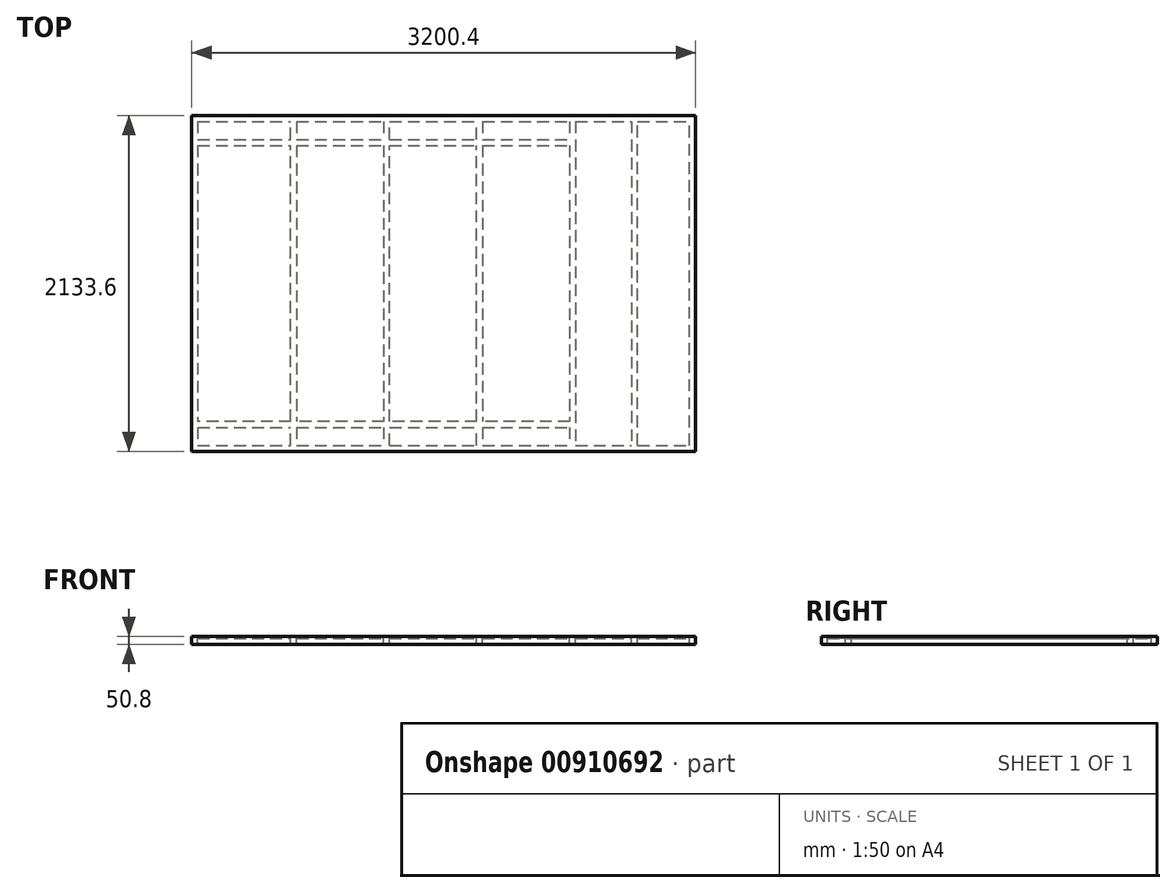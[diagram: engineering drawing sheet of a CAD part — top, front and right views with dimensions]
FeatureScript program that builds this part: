
annotation { "Feature Type Name" : "Feature", "Feature Type Description" : "" }
export const myFeature = defineFeature(function(context is Context, id is Id, definition is map)
    precondition{}
    {
        {
            var Q0;
            Q0=qCreatedBy(makeId("Top.planeOp"),FACE);
            var sketch = newSketch(context, id + "F0", { "sketchPlane" : qUnion([Q0])});
            skLineSegment(sketch, "E0.bottom", {"start": v(1600.2, 1066.8) * mm, "end": v(-1600.2, 1066.8) * mm});
            skLineSegment(sketch, "E0.top", {"start": v(1600.2, -1066.8) * mm, "end": v(-1600.2, -1066.8) * mm});
            skLineSegment(sketch, "E0.left", {"start": v(1600.2, 1066.8) * mm, "end": v(1600.2, -1066.8) * mm});
            skLineSegment(sketch, "E0.right", {"start": v(-1600.2, 1066.8) * mm, "end": v(-1600.2, -1066.8) * mm});
            skPoint(sketch, "E0.middle", {"position": v(0, 0) * mm});
            skLineSegment(sketch, "E1", {"start": v(-1600.2, -1066.8) * mm, "end": v(-381, -1066.8) * mm});
            skLineSegment(sketch, "E2", {"start": v(-381, -1066.8) * mm, "end": v(-381, -1028.7) * mm});
            skLineSegment(sketch, "E3", {"start": v(-381, 1066.8) * mm, "end": v(838.2, 1066.8) * mm});
            skLineSegment(sketch, "E4", {"start": v(838.2, 1066.8) * mm, "end": v(838.2, -1028.7) * mm});
            skLineSegment(sketch, "E5", {"start": v(-1600.2, -1028.7) * mm, "end": v(1600.2, -1028.7) * mm});
            skLineSegment(sketch, "E6", {"start": v(-1600.2, 1028.7) * mm, "end": v(1600.2, 1028.7) * mm});
            skLineSegment(sketch, "E7", {"start": v(-1562.1, 1028.7) * mm, "end": v(-1562.1, 914.4) * mm});
            skLineSegment(sketch, "E8", {"start": v(1562.1, -1028.7) * mm, "end": v(1562.1, 1028.7) * mm});
            skLineSegment(sketch, "E9", {"start": v(-1600.2, -1028.7) * mm, "end": v(-971.55, -1028.7) * mm});
            skLineSegment(sketch, "E10", {"start": v(-971.55, -1028.7) * mm, "end": v(-971.55, -914.4) * mm});
            skLineSegment(sketch, "E11", {"start": v(-933.45, 1028.7) * mm, "end": v(-933.45, 914.4) * mm});
            skLineSegment(sketch, "E12", {"start": v(-1600.2, 914.4) * mm, "end": v(838.2, 914.4) * mm});
            skLineSegment(sketch, "E13", {"start": v(-1600.2, 876.3) * mm, "end": v(838.2, 876.3) * mm});
            skLineSegment(sketch, "E14.trimOffspring", {"start": v(-971.55, 914.4) * mm, "end": v(-971.55, 1028.7) * mm});
            skLineSegment(sketch, "E15.trimOffspring", {"start": v(-933.45, 876.3) * mm, "end": v(-933.45, -876.3) * mm});
            skLineSegment(sketch, "E16.trimOffspring", {"start": v(-1562.1, 876.3) * mm, "end": v(-1562.1, -876.3) * mm});
            skLineSegment(sketch, "E17", {"start": v(-1600.2, -914.4) * mm, "end": v(838.2, -914.4) * mm});
            skLineSegment(sketch, "E18", {"start": v(838.2, -876.3) * mm, "end": v(-1600.2, -876.3) * mm});
            skLineSegment(sketch, "E19.trimOffspring", {"start": v(-933.45, -914.4) * mm, "end": v(-933.45, -1028.7) * mm});
            skLineSegment(sketch, "E20.trimOffspring", {"start": v(-971.55, -876.3) * mm, "end": v(-971.55, 876.3) * mm});
            skLineSegment(sketch, "E21.trimOffspring", {"start": v(-1562.1, -914.4) * mm, "end": v(-1562.1, -1028.7) * mm});
            skLineSegment(sketch, "E22", {"start": v(800.1, 1028.7) * mm, "end": v(800.1, 914.4) * mm});
            skLineSegment(sketch, "E23", {"start": v(247.65, 1028.7) * mm, "end": v(247.65, 914.4) * mm});
            skLineSegment(sketch, "E24", {"start": v(209.55, -1028.7) * mm, "end": v(209.55, -914.4) * mm});
            skLineSegment(sketch, "E25", {"start": v(-381, 1028.7) * mm, "end": v(-381, 914.4) * mm});
            skLineSegment(sketch, "E26", {"start": v(-342.9, -1028.7) * mm, "end": v(-342.9, -914.4) * mm});
            skLineSegment(sketch, "E27.trimOffspring", {"start": v(-381, 876.3) * mm, "end": v(-381, -876.3) * mm});
            skLineSegment(sketch, "E28.trimOffspring", {"start": v(-342.9, 914.4) * mm, "end": v(-342.9, 1028.7) * mm});
            skLineSegment(sketch, "E29.trimOffspring", {"start": v(-381, -914.4) * mm, "end": v(-381, -1028.7) * mm});
            skLineSegment(sketch, "E30.trimOffspring", {"start": v(-342.9, -876.3) * mm, "end": v(-342.9, 876.3) * mm});
            skLineSegment(sketch, "E31.trimOffspring", {"start": v(247.65, -914.4) * mm, "end": v(247.65, -1028.7) * mm});
            skLineSegment(sketch, "E32.trimOffspring", {"start": v(209.55, -876.3) * mm, "end": v(209.55, 876.3) * mm});
            skLineSegment(sketch, "E33.trimOffspring", {"start": v(800.1, -914.4) * mm, "end": v(800.1, -1028.7) * mm});
            skLineSegment(sketch, "E34.trimOffspring", {"start": v(209.55, 914.4) * mm, "end": v(209.55, 1028.7) * mm});
            skLineSegment(sketch, "E35.trimOffspring", {"start": v(247.65, 876.3) * mm, "end": v(247.65, -876.3) * mm});
            skLineSegment(sketch, "E36.trimOffspring", {"start": v(800.1, 876.3) * mm, "end": v(800.1, -876.3) * mm});
            skLineSegment(sketch, "E37", {"start": v(1231.9, -1028.7) * mm, "end": v(1231.9, 1028.7) * mm});
            skLineSegment(sketch, "E38", {"start": v(1231.9, 1028.7) * mm, "end": v(1193.8, 1028.7) * mm});
            skLineSegment(sketch, "E39", {"start": v(1193.8, 1028.7) * mm, "end": v(1193.8, -1028.7) * mm});
            skSolve(sketch);
        }
        {
            var Q0;
            {var subQ5=sQuery(id+"F0.wireOp",EDGE,"E7");Q0=makeQuery(id+"F0.imprint","IMPRINT",FACE,{"disambiguationData":[TD([[makeQuery(id+"F0.imprint","IMPRINT",EDGE,{"derivedFrom":subQ5}),-1.0]])]});}
            var Q1;
            {var subQ5=sQuery(id+"F0.wireOp",EDGE,"E16.trimOffspring");Q1=makeQuery(id+"F0.imprint","IMPRINT",FACE,{"disambiguationData":[TD([[makeQuery(id+"F0.imprint","IMPRINT",EDGE,{"derivedFrom":subQ5}),-1.0]])]});}
            var Q2;
            {var subQ5=sQuery(id+"F0.wireOp",EDGE,"E21.trimOffspring");Q2=makeQuery(id+"F0.imprint","IMPRINT",FACE,{"disambiguationData":[TD([[makeQuery(id+"F0.imprint","IMPRINT",EDGE,{"derivedFrom":subQ5}),-1.0]])]});}
            var Q3;
            {var subQ1=sQuery(id+"F0.wireOp",EDGE,"E4");var subQ4=sQuery(id+"F0.wireOp",EDGE,"E0.bottom");var subQ5=makeQuery(id+"F0.imprint","INTERSECT",VERTEX,{"derivedFrom":[subQ4,subQ1]});Q3=makeQuery(id+"F0.imprint","IMPRINT",FACE,{"disambiguationData":[TD([[makeQuery(id+"F0.imprint","IMPRINT",EDGE,{"disambiguationData":[TD([[subQ5,1.0]])],"derivedFrom":subQ4}),1.0]])]});}
            var Q4;
            {var subQ3=sQuery(id+"F0.wireOp",EDGE,"E2");Q4=makeQuery(id+"F0.imprint","IMPRINT",FACE,{"disambiguationData":[TD([[makeQuery(id+"F0.imprint","IMPRINT",EDGE,{"derivedFrom":subQ3}),1.0]])]});}
            var Q5;
            {var subQ12=sQuery(id+"F0.wireOp",EDGE,"E0.bottom");var subQ14=makeQuery(id+"F0.imprint","IMPRINT",VERTEX,{"derivedFrom":subQ12});Q5=makeQuery(id+"F0.imprint","IMPRINT",FACE,{"disambiguationData":[TD([[makeQuery(id+"F0.imprint","IMPRINT",EDGE,{"disambiguationData":[TD([[subQ14,-1.0]])],"derivedFrom":subQ12}),1.0]])]});}
            var Q6;
            {var subQ3=sQuery(id+"F0.wireOp",EDGE,"E2");Q6=makeQuery(id+"F0.imprint","IMPRINT",FACE,{"disambiguationData":[TD([[makeQuery(id+"F0.imprint","IMPRINT",EDGE,{"derivedFrom":subQ3}),-1.0]])]});}
            var Q7;
            {var subQ2=sQuery(id+"F0.wireOp",EDGE,"E0.right");var subQ6=sQuery(id+"F0.wireOp",EDGE,"E13");var subQ7=makeQuery(id+"F0.imprint","INTERSECT",VERTEX,{"derivedFrom":[subQ2,subQ6]});Q7=makeQuery(id+"F0.imprint","IMPRINT",FACE,{"disambiguationData":[TD([[makeQuery(id+"F0.imprint","IMPRINT",EDGE,{"disambiguationData":[TD([[subQ7,1.0]])],"derivedFrom":subQ2}),1.0]])]});}
            var Q8;
            {var subQ3=sQuery(id+"F0.wireOp",EDGE,"E18");var subQ4=sQuery(id+"F0.wireOp",EDGE,"E0.right");var subQ5=makeQuery(id+"F0.imprint","INTERSECT",VERTEX,{"derivedFrom":[subQ4,subQ3]});Q8=makeQuery(id+"F0.imprint","IMPRINT",FACE,{"disambiguationData":[TD([[makeQuery(id+"F0.imprint","IMPRINT",EDGE,{"disambiguationData":[TD([[subQ5,-1.0]])],"derivedFrom":subQ4}),1.0]])]});}
            var Q9;
            {var subQ0=sQuery(id+"F0.wireOp",EDGE,"E16.trimOffspring");Q9=makeQuery(id+"F0.imprint","IMPRINT",FACE,{"disambiguationData":[TD([[makeQuery(id+"F0.imprint","IMPRINT",EDGE,{"derivedFrom":subQ0}),1.0]])]});}
            var Q10;
            {var subQ0=sQuery(id+"F0.wireOp",EDGE,"E15.trimOffspring");Q10=makeQuery(id+"F0.imprint","IMPRINT",FACE,{"disambiguationData":[TD([[makeQuery(id+"F0.imprint","IMPRINT",EDGE,{"derivedFrom":subQ0}),1.0]])]});}
            var Q11;
            {var subQ0=sQuery(id+"F0.wireOp",EDGE,"E30.trimOffspring");Q11=makeQuery(id+"F0.imprint","IMPRINT",FACE,{"disambiguationData":[TD([[makeQuery(id+"F0.imprint","IMPRINT",EDGE,{"derivedFrom":subQ0}),-1.0]])]});}
            var Q12;
            {var subQ8=sQuery(id+"F0.wireOp",EDGE,"E39");Q12=makeQuery(id+"F0.imprint","IMPRINT",FACE,{"disambiguationData":[TD([[makeQuery(id+"F0.imprint","IMPRINT",EDGE,{"derivedFrom":subQ8}),-1.0]])]});}
            var Q13;
            {var subQ5=sQuery(id+"F0.wireOp",EDGE,"E22");Q13=makeQuery(id+"F0.imprint","IMPRINT",FACE,{"disambiguationData":[TD([[makeQuery(id+"F0.imprint","IMPRINT",EDGE,{"derivedFrom":subQ5}),1.0]])]});}
            var Q14;
            {var subQ0=sQuery(id+"F0.wireOp",EDGE,"E22");Q14=makeQuery(id+"F0.imprint","IMPRINT",FACE,{"disambiguationData":[TD([[makeQuery(id+"F0.imprint","IMPRINT",EDGE,{"derivedFrom":subQ0}),-1.0]])]});}
            var Q15;
            {var subQ0=sQuery(id+"F0.wireOp",EDGE,"E23");Q15=makeQuery(id+"F0.imprint","IMPRINT",FACE,{"disambiguationData":[TD([[makeQuery(id+"F0.imprint","IMPRINT",EDGE,{"derivedFrom":subQ0}),-1.0]])]});}
            var Q16;
            {var subQ0=sQuery(id+"F0.wireOp",EDGE,"E28.trimOffspring");Q16=makeQuery(id+"F0.imprint","IMPRINT",FACE,{"disambiguationData":[TD([[makeQuery(id+"F0.imprint","IMPRINT",EDGE,{"derivedFrom":subQ0}),-1.0]])]});}
            var Q17;
            {var subQ0=sQuery(id+"F0.wireOp",EDGE,"E25");Q17=makeQuery(id+"F0.imprint","IMPRINT",FACE,{"disambiguationData":[TD([[makeQuery(id+"F0.imprint","IMPRINT",EDGE,{"derivedFrom":subQ0}),1.0]])]});}
            var Q18;
            {var subQ0=sQuery(id+"F0.wireOp",EDGE,"E7");Q18=makeQuery(id+"F0.imprint","IMPRINT",FACE,{"disambiguationData":[TD([[makeQuery(id+"F0.imprint","IMPRINT",EDGE,{"derivedFrom":subQ0}),1.0]])]});}
            var Q19;
            {var subQ0=sQuery(id+"F0.wireOp",EDGE,"E15.trimOffspring");Q19=makeQuery(id+"F0.imprint","IMPRINT",FACE,{"disambiguationData":[TD([[makeQuery(id+"F0.imprint","IMPRINT",EDGE,{"derivedFrom":subQ0}),-1.0]])]});}
            var Q20;
            {var subQ0=sQuery(id+"F0.wireOp",EDGE,"E11");Q20=makeQuery(id+"F0.imprint","IMPRINT",FACE,{"disambiguationData":[TD([[makeQuery(id+"F0.imprint","IMPRINT",EDGE,{"derivedFrom":subQ0}),-1.0]])]});}
            var Q21;
            {var subQ0=sQuery(id+"F0.wireOp",EDGE,"E11");Q21=makeQuery(id+"F0.imprint","IMPRINT",FACE,{"disambiguationData":[TD([[makeQuery(id+"F0.imprint","IMPRINT",EDGE,{"derivedFrom":subQ0}),1.0]])]});}
            var Q22;
            {var subQ0=sQuery(id+"F0.wireOp",EDGE,"E27.trimOffspring");Q22=makeQuery(id+"F0.imprint","IMPRINT",FACE,{"disambiguationData":[TD([[makeQuery(id+"F0.imprint","IMPRINT",EDGE,{"derivedFrom":subQ0}),1.0]])]});}
            var Q23;
            {var subQ0=sQuery(id+"F0.wireOp",EDGE,"E32.trimOffspring");Q23=makeQuery(id+"F0.imprint","IMPRINT",FACE,{"disambiguationData":[TD([[makeQuery(id+"F0.imprint","IMPRINT",EDGE,{"derivedFrom":subQ0}),-1.0]])]});}
            var Q24;
            {var subQ5=sQuery(id+"F0.wireOp",EDGE,"E36.trimOffspring");Q24=makeQuery(id+"F0.imprint","IMPRINT",FACE,{"disambiguationData":[TD([[makeQuery(id+"F0.imprint","IMPRINT",EDGE,{"derivedFrom":subQ5}),1.0]])]});}
            var Q25;
            {var subQ0=sQuery(id+"F0.wireOp",EDGE,"E35.trimOffspring");Q25=makeQuery(id+"F0.imprint","IMPRINT",FACE,{"disambiguationData":[TD([[makeQuery(id+"F0.imprint","IMPRINT",EDGE,{"derivedFrom":subQ0}),1.0]])]});}
            var Q26;
            {var subQ0=sQuery(id+"F0.wireOp",EDGE,"E31.trimOffspring");Q26=makeQuery(id+"F0.imprint","IMPRINT",FACE,{"disambiguationData":[TD([[makeQuery(id+"F0.imprint","IMPRINT",EDGE,{"derivedFrom":subQ0}),1.0]])]});}
            var Q27;
            {var subQ0=sQuery(id+"F0.wireOp",EDGE,"E37");Q27=makeQuery(id+"F0.imprint","IMPRINT",FACE,{"disambiguationData":[TD([[makeQuery(id+"F0.imprint","IMPRINT",EDGE,{"derivedFrom":subQ0}),1.0]])]});}
            var Q28;
            {var subQ5=sQuery(id+"F0.wireOp",EDGE,"E8");Q28=makeQuery(id+"F0.imprint","IMPRINT",FACE,{"disambiguationData":[TD([[makeQuery(id+"F0.imprint","IMPRINT",EDGE,{"derivedFrom":subQ5}),-1.0]])]});}
            var Q29;
            {var subQ0=sQuery(id+"F0.wireOp",EDGE,"E8");Q29=makeQuery(id+"F0.imprint","IMPRINT",FACE,{"disambiguationData":[TD([[makeQuery(id+"F0.imprint","IMPRINT",EDGE,{"derivedFrom":subQ0}),1.0]])]});}
            var Q30;
            {var subQ0=sQuery(id+"F0.wireOp",EDGE,"E10");Q30=makeQuery(id+"F0.imprint","IMPRINT",FACE,{"disambiguationData":[TD([[makeQuery(id+"F0.imprint","IMPRINT",EDGE,{"derivedFrom":subQ0}),-1.0]])]});}
            var Q31;
            {var subQ2=sQuery(id+"F0.wireOp",EDGE,"E26");Q31=makeQuery(id+"F0.imprint","IMPRINT",FACE,{"disambiguationData":[TD([[makeQuery(id+"F0.imprint","IMPRINT",EDGE,{"derivedFrom":subQ2}),1.0]])]});}
            var Q32;
            {var subQ2=sQuery(id+"F0.wireOp",EDGE,"E24");Q32=makeQuery(id+"F0.imprint","IMPRINT",FACE,{"disambiguationData":[TD([[makeQuery(id+"F0.imprint","IMPRINT",EDGE,{"derivedFrom":subQ2}),-1.0]])]});}
            var Q33;
            {var subQ5=sQuery(id+"F0.wireOp",EDGE,"E33.trimOffspring");Q33=makeQuery(id+"F0.imprint","IMPRINT",FACE,{"disambiguationData":[TD([[makeQuery(id+"F0.imprint","IMPRINT",EDGE,{"derivedFrom":subQ5}),1.0]])]});}
            var Q34;
            {var subQ0=sQuery(id+"F0.wireOp",EDGE,"E24");Q34=makeQuery(id+"F0.imprint","IMPRINT",FACE,{"disambiguationData":[TD([[makeQuery(id+"F0.imprint","IMPRINT",EDGE,{"derivedFrom":subQ0}),1.0]])]});}
            var Q35;
            {var subQ2=sQuery(id+"F0.wireOp",EDGE,"E19.trimOffspring");Q35=makeQuery(id+"F0.imprint","IMPRINT",FACE,{"disambiguationData":[TD([[makeQuery(id+"F0.imprint","IMPRINT",EDGE,{"derivedFrom":subQ2}),1.0]])]});}
            var Q36;
            {var subQ2=sQuery(id+"F0.wireOp",EDGE,"E10");Q36=makeQuery(id+"F0.imprint","IMPRINT",FACE,{"disambiguationData":[TD([[makeQuery(id+"F0.imprint","IMPRINT",EDGE,{"derivedFrom":subQ2}),1.0]])]});}
            extrude(context, id + "F1", {"entities" : qUnion([Q0, Q1, Q2, Q3, Q4, Q5, Q6, Q7, Q8, Q9, Q10, Q11, Q12, Q13, Q14, Q15, Q16, Q17, Q18, Q19, Q20, Q21, Q22, Q23, Q24, Q25, Q26, Q27, Q28, Q29, Q30, Q31, Q32, Q33, Q34, Q35, Q36]), "depth" : 12.7 * mm, "offsetDistance" : 25.4 * mm});
        }
        {
            var Q0;
            {var subQ1=sQuery(id+"F0.wireOp",EDGE,"E7");var subQ3=sQuery(id+"F0.wireOp",EDGE,"E0.right");var subQ10=sQuery(id+"F0.wireOp",EDGE,"E13");var subQ11=makeQuery(id+"F0.imprint","INTERSECT",VERTEX,{"derivedFrom":[subQ3,subQ10]});var subQ22=sQuery(id+"F0.wireOp",EDGE,"E4");var subQ25=sQuery(id+"F0.wireOp",EDGE,"E16.trimOffspring");var subQ53=sQuery(id+"F0.wireOp",EDGE,"E0.bottom");var subQ55=makeQuery(id+"F0.imprint","IMPRINT",VERTEX,{"derivedFrom":subQ53});var subQ57=makeQuery(id+"F0.imprint","INTERSECT",VERTEX,{"derivedFrom":[subQ53,subQ22]});var subQ64=sQuery(id+"F0.wireOp",EDGE,"E8");var subQ69=sQuery(id+"F0.wireOp",EDGE,"E18");var subQ70=makeQuery(id+"F0.imprint","INTERSECT",VERTEX,{"derivedFrom":[subQ3,subQ69]});var subQ77=sQuery(id+"F0.wireOp",EDGE,"E2");var subQ92=makeQuery(id+"F0.imprint","IMPRINT",EDGE,{"derivedFrom":subQ77});var subQ105=sQuery(id+"F0.wireOp",EDGE,"E21.trimOffspring");Q0=qUnion([makeQuery(id+"F0.imprint","IMPRINT",FACE,{"disambiguationData":[TD([[subQ92,1.0]])]}),makeQuery(id+"F0.imprint","IMPRINT",FACE,{"disambiguationData":[TD([[makeQuery(id+"F0.imprint","IMPRINT",EDGE,{"derivedFrom":subQ105}),-1.0]])]}),makeQuery(id+"F0.imprint","IMPRINT",FACE,{"disambiguationData":[TD([[makeQuery(id+"F0.imprint","IMPRINT",EDGE,{"disambiguationData":[TD([[subQ70,-1.0]])],"derivedFrom":subQ3}),1.0]])]}),makeQuery(id+"F0.imprint","IMPRINT",FACE,{"disambiguationData":[TD([[makeQuery(id+"F0.imprint","IMPRINT",EDGE,{"derivedFrom":subQ64}),-1.0]])]}),makeQuery(id+"F0.imprint","IMPRINT",FACE,{"disambiguationData":[TD([[subQ92,-1.0]])]}),makeQuery(id+"F0.imprint","IMPRINT",FACE,{"disambiguationData":[TD([[makeQuery(id+"F0.imprint","IMPRINT",EDGE,{"derivedFrom":subQ25}),-1.0]])]}),makeQuery(id+"F0.imprint","IMPRINT",FACE,{"disambiguationData":[TD([[makeQuery(id+"F0.imprint","IMPRINT",EDGE,{"disambiguationData":[TD([[subQ57,1.0]])],"derivedFrom":subQ53}),1.0]])]}),makeQuery(id+"F0.imprint","IMPRINT",FACE,{"disambiguationData":[TD([[makeQuery(id+"F0.imprint","IMPRINT",EDGE,{"disambiguationData":[TD([[subQ55,-1.0]])],"derivedFrom":subQ53}),1.0]])]}),makeQuery(id+"F0.imprint","IMPRINT",FACE,{"disambiguationData":[TD([[makeQuery(id+"F0.imprint","IMPRINT",EDGE,{"derivedFrom":subQ1}),-1.0]])]}),makeQuery(id+"F0.imprint","IMPRINT",FACE,{"disambiguationData":[TD([[makeQuery(id+"F0.imprint","IMPRINT",EDGE,{"disambiguationData":[TD([[subQ11,1.0]])],"derivedFrom":subQ3}),1.0]])]})]);}
            var Q1;
            {var subQ0=sQuery(id+"F0.wireOp",EDGE,"E10");Q1=makeQuery(id+"F0.imprint","IMPRINT",FACE,{"disambiguationData":[TD([[makeQuery(id+"F0.imprint","IMPRINT",EDGE,{"derivedFrom":subQ0}),-1.0]])]});}
            var Q2;
            {var subQ0=sQuery(id+"F0.wireOp",EDGE,"E15.trimOffspring");Q2=makeQuery(id+"F0.imprint","IMPRINT",FACE,{"disambiguationData":[TD([[makeQuery(id+"F0.imprint","IMPRINT",EDGE,{"derivedFrom":subQ0}),-1.0]])]});}
            var Q3;
            {var subQ0=sQuery(id+"F0.wireOp",EDGE,"E11");Q3=makeQuery(id+"F0.imprint","IMPRINT",FACE,{"disambiguationData":[TD([[makeQuery(id+"F0.imprint","IMPRINT",EDGE,{"derivedFrom":subQ0}),-1.0]])]});}
            var Q4;
            {var subQ0=sQuery(id+"F0.wireOp",EDGE,"E25");Q4=makeQuery(id+"F0.imprint","IMPRINT",FACE,{"disambiguationData":[TD([[makeQuery(id+"F0.imprint","IMPRINT",EDGE,{"derivedFrom":subQ0}),1.0]])]});}
            var Q5;
            {var subQ0=sQuery(id+"F0.wireOp",EDGE,"E27.trimOffspring");Q5=makeQuery(id+"F0.imprint","IMPRINT",FACE,{"disambiguationData":[TD([[makeQuery(id+"F0.imprint","IMPRINT",EDGE,{"derivedFrom":subQ0}),1.0]])]});}
            var Q6;
            {var subQ2=sQuery(id+"F0.wireOp",EDGE,"E26");Q6=makeQuery(id+"F0.imprint","IMPRINT",FACE,{"disambiguationData":[TD([[makeQuery(id+"F0.imprint","IMPRINT",EDGE,{"derivedFrom":subQ2}),1.0]])]});}
            var Q7;
            {var subQ2=sQuery(id+"F0.wireOp",EDGE,"E24");Q7=makeQuery(id+"F0.imprint","IMPRINT",FACE,{"disambiguationData":[TD([[makeQuery(id+"F0.imprint","IMPRINT",EDGE,{"derivedFrom":subQ2}),-1.0]])]});}
            var Q8;
            {var subQ0=sQuery(id+"F0.wireOp",EDGE,"E32.trimOffspring");Q8=makeQuery(id+"F0.imprint","IMPRINT",FACE,{"disambiguationData":[TD([[makeQuery(id+"F0.imprint","IMPRINT",EDGE,{"derivedFrom":subQ0}),-1.0]])]});}
            var Q9;
            {var subQ5=sQuery(id+"F0.wireOp",EDGE,"E36.trimOffspring");Q9=makeQuery(id+"F0.imprint","IMPRINT",FACE,{"disambiguationData":[TD([[makeQuery(id+"F0.imprint","IMPRINT",EDGE,{"derivedFrom":subQ5}),1.0]])]});}
            var Q10;
            {var subQ5=sQuery(id+"F0.wireOp",EDGE,"E33.trimOffspring");Q10=makeQuery(id+"F0.imprint","IMPRINT",FACE,{"disambiguationData":[TD([[makeQuery(id+"F0.imprint","IMPRINT",EDGE,{"derivedFrom":subQ5}),1.0]])]});}
            var Q11;
            {var subQ0=sQuery(id+"F0.wireOp",EDGE,"E37");Q11=makeQuery(id+"F0.imprint","IMPRINT",FACE,{"disambiguationData":[TD([[makeQuery(id+"F0.imprint","IMPRINT",EDGE,{"derivedFrom":subQ0}),1.0]])]});}
            var Q12;
            {var subQ5=sQuery(id+"F0.wireOp",EDGE,"E22");Q12=makeQuery(id+"F0.imprint","IMPRINT",FACE,{"disambiguationData":[TD([[makeQuery(id+"F0.imprint","IMPRINT",EDGE,{"derivedFrom":subQ5}),1.0]])]});}
            var Q13;
            {var subQ0=sQuery(id+"F0.wireOp",EDGE,"E23");Q13=makeQuery(id+"F0.imprint","IMPRINT",FACE,{"disambiguationData":[TD([[makeQuery(id+"F0.imprint","IMPRINT",EDGE,{"derivedFrom":subQ0}),-1.0]])]});}
            extrude(context, id + "F2", {"entities" : qUnion([Q0, Q1, Q2, Q3, Q4, Q5, Q6, Q7, Q8, Q9, Q10, Q11, Q12, Q13]), "operationType" : NewBodyOperationType.ADD, "oppositeDirection" : true, "depth" : 38.1 * mm, "offsetDistance" : 25.4 * mm});
        }
    });
